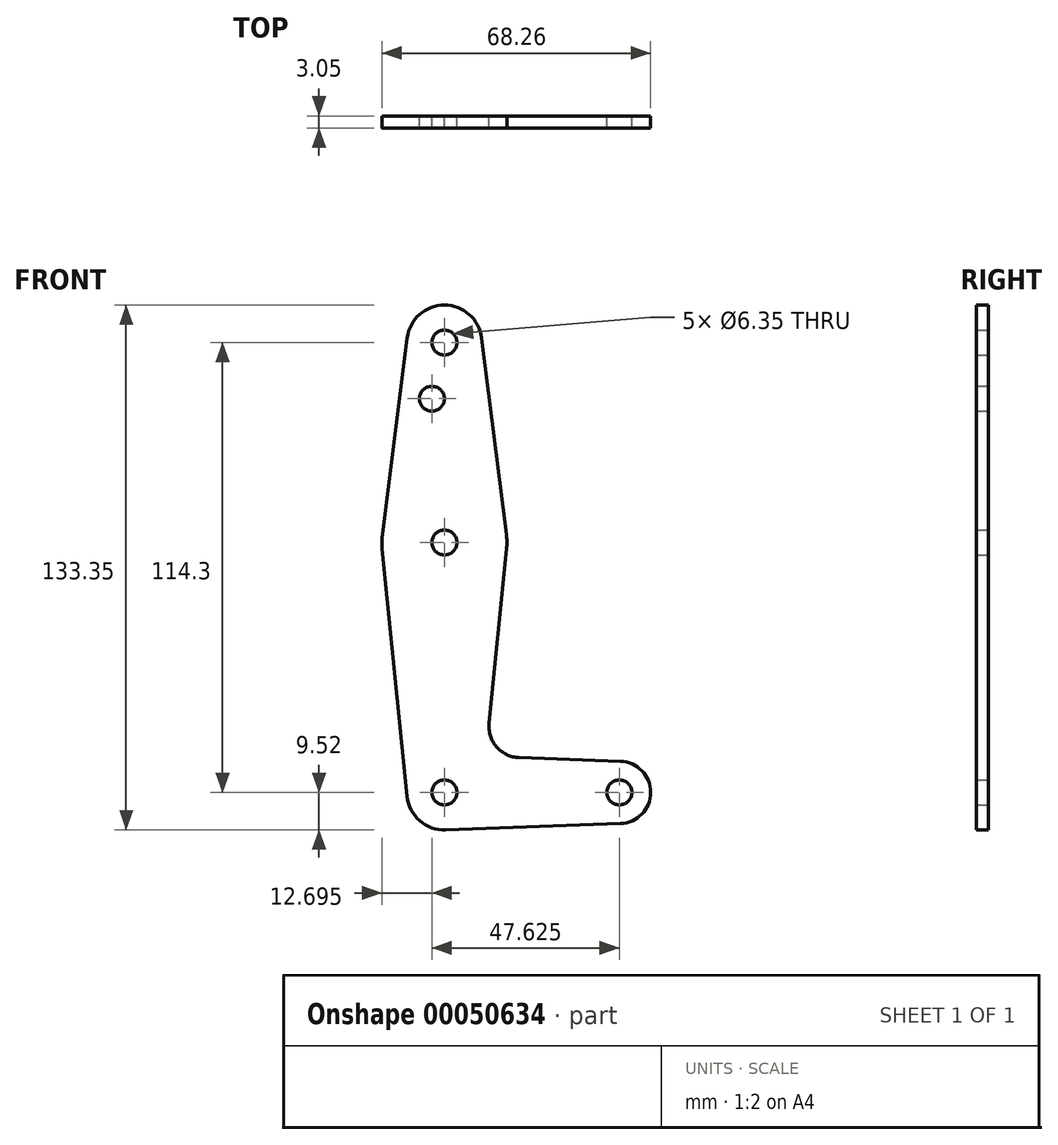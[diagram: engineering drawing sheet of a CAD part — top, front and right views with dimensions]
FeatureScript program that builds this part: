
annotation { "Feature Type Name" : "Feature", "Feature Type Description" : "" }
export const myFeature = defineFeature(function(context is Context, id is Id, definition is map)
    precondition{}
    {
        {
            var Q0;
            Q0=qCreatedBy(makeId("Front.planeOp"),FACE);
            var sketch = newSketch(context, id + "F0", { "sketchPlane" : qUnion([Q0])});
            skLineSegment(sketch, "E0", {"start": v(0, 0) * mm, "end": v(44.45, 0) * mm, "construction": true});
            skLineSegment(sketch, "E1", {"start": v(0, 0) * mm, "end": v(0, 114.3) * mm, "construction": true});
            skCircle(sketch, "E2", {"center": v(0, 0) * mm, "radius": 9.53 * mm});
            skCircle(sketch, "E3", {"center": v(44.45, 0) * mm, "radius": 7.94 * mm});
            skCircle(sketch, "E4", {"center": v(0, 114.3) * mm, "radius": 9.53 * mm});
            skCircle(sketch, "E5", {"center": v(0, 63.5) * mm, "radius": 15.88 * mm});
            skLineSegment(sketch, "E6", {"start": v(-9.45, 115.5) * mm, "end": v(-15.75, 65.48) * mm});
            skLineSegment(sketch, "E7", {"start": v(0.34, -9.52) * mm, "end": v(44.73, -7.93) * mm});
            skLineSegment(sketch, "E8", {"start": v(44.73, 7.93) * mm, "end": v(18.97, 8.85) * mm});
            skLineSegment(sketch, "E9", {"start": v(15.8, 61.91) * mm, "end": v(11.34, 17.6) * mm});
            skLineSegment(sketch, "E10", {"start": v(9.45, 115.5) * mm, "end": v(15.8, 65.13) * mm});
            skCircle(sketch, "E11", {"center": v(0, 114.3) * mm, "radius": 3.18 * mm});
            skCircle(sketch, "E12", {"center": v(0, 63.5) * mm, "radius": 3.18 * mm});
            skCircle(sketch, "E13", {"center": v(0, 0) * mm, "radius": 3.18 * mm});
            skCircle(sketch, "E14", {"center": v(44.45, 0) * mm, "radius": 3.18 * mm});
            skCircle(sketch, "E15", {"center": v(-3.18, 100.03) * mm, "radius": 3.18 * mm});
            skArc(sketch, "E16.filletArc", {"start": v(11.34, 17.6) * mm, "mid": v(13.26, 11.57) * mm, "end": v(18.97, 8.85) * mm});
            skLineSegment(sketch, "E17", {"start": v(-15.8, 61.91) * mm, "end": v(-9.48, -0.95) * mm});
            skSolve(sketch);
        }
        {
            var Q0;
            Q0 = qSketchRegion(id + "F0", true);
            extrude(context, id + "F1", {"entities" : qUnion([Q0]), "depth" : 3.05 * mm});
        }
    });
